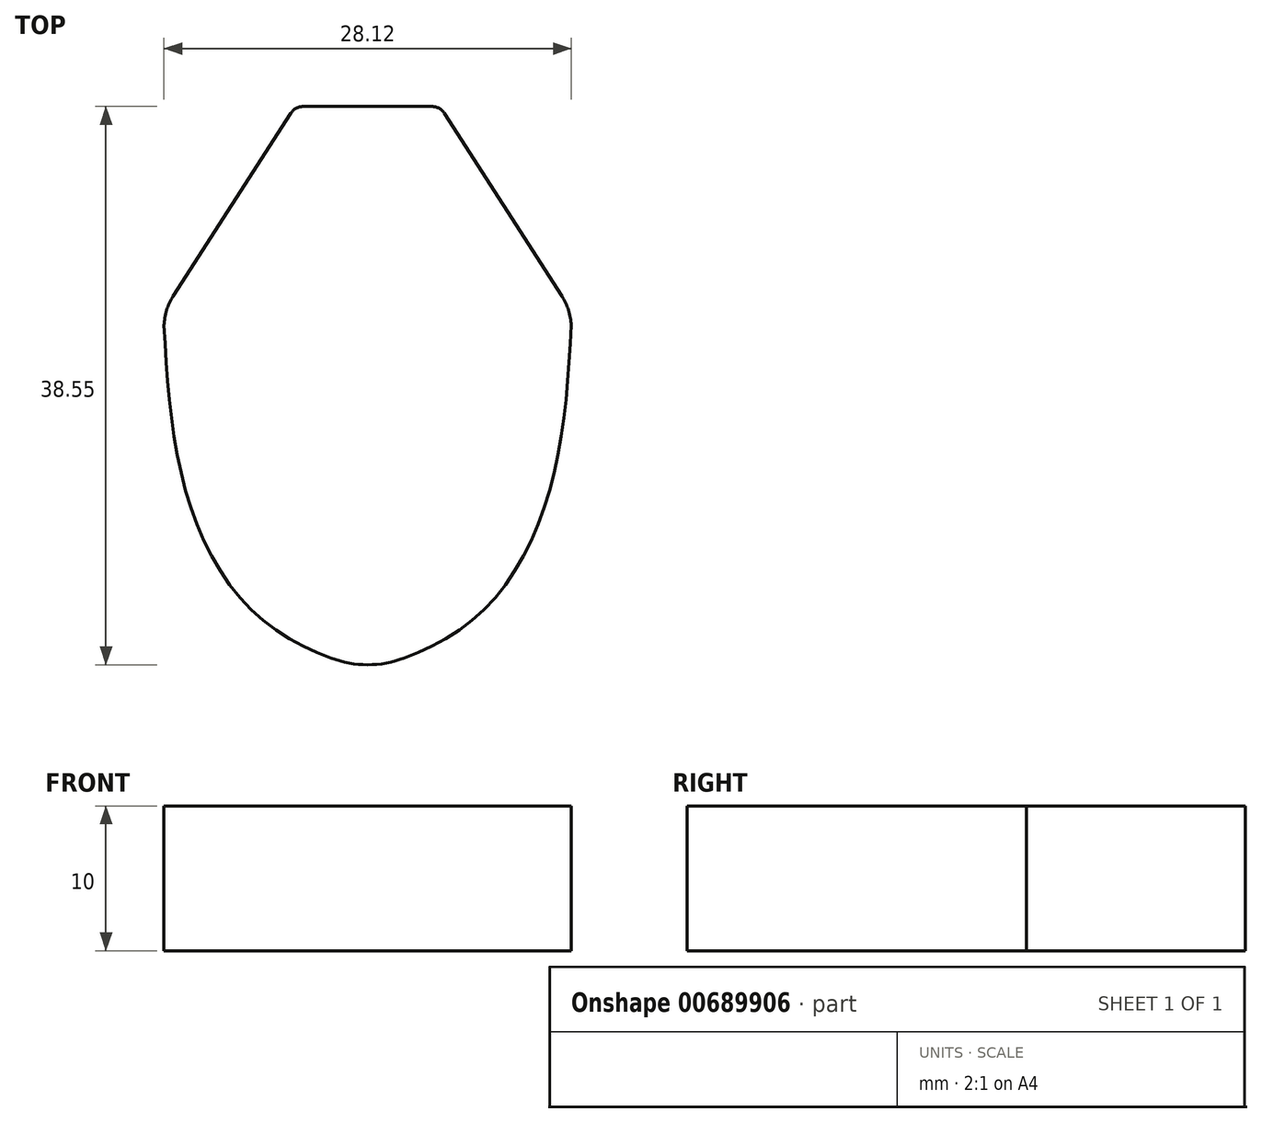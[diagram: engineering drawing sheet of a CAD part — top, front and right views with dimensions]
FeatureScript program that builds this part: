
annotation { "Feature Type Name" : "Feature", "Feature Type Description" : "" }
export const myFeature = defineFeature(function(context is Context, id is Id, definition is map)
    precondition{}
    {
        {
            var Q0;
            Q0=qCreatedBy(makeId("Top.planeOp"),FACE);
            var sketch = newSketch(context, id + "F0", { "sketchPlane" : qUnion([Q0])});
            skLineSegment(sketch, "E0", {"start": v(-13.42, 25.9) * mm, "end": v(-5.3, 38.54) * mm});
            skPoint(sketch, "E1.visualSharp", {"position": v(-5, 39) * mm});
            skArc(sketch, "E1.filletArc", {"start": v(-4.45, 39) * mm, "mid": v(-4.93, 38.88) * mm, "end": v(-5.3, 38.54) * mm});
            skPoint(sketch, "E2.visualSharp", {"position": v(-14, 25) * mm});
            skArc(sketch, "E2.filletArc", {"start": v(-13.42, 25.9) * mm, "mid": v(-13.88, 24.93) * mm, "end": v(-14.06, 23.89) * mm});
            skFitSpline(sketch, "E3", {"points": [v(-14.06, 23.89) * mm, v(-12.32, 11.64) * mm, v(-6.8, 3.17) * mm, v(0, 0) * mm], "startDerivative": vector(1.56, -32.92) * mm, "endDerivative": vector(18.5, -6.76) * mm});
            skArc(sketch, "E4.MirrorCS", {"start": v(13.42, 25.9) * mm, "mid": v(13.88, 24.93) * mm, "end": v(14.06, 23.89) * mm});
            skArc(sketch, "E5.MirrorCS", {"start": v(4.45, 39) * mm, "mid": v(4.93, 38.88) * mm, "end": v(5.3, 38.54) * mm});
            skFitSpline(sketch, "E6.MirrorCS", {"points": [v(14.06, 23.89) * mm, v(12.32, 11.64) * mm, v(6.8, 3.17) * mm, v(0, 0) * mm], "startDerivative": vector(-1.56, -32.92) * mm, "endDerivative": vector(-18.5, -6.76) * mm});
            skPoint(sketch, "E7.MirrorP", {"position": v(5, 39) * mm});
            skPoint(sketch, "E8.MirrorP", {"position": v(14, 25) * mm});
            skLineSegment(sketch, "E9.MirrorCS", {"start": v(13.42, 25.9) * mm, "end": v(5.3, 38.54) * mm});
            skLineSegment(sketch, "E10", {"start": v(-4.45, 39) * mm, "end": v(4.45, 39) * mm});
            skSolve(sketch);
        }
        {
            var Q0;
            Q0=makeQuery(id+"F0.imprint","IMPRINT",FACE,{"disambiguationData":[TD([[makeQuery(id+"F0.imprint","IMPRINT",EDGE,{"derivedFrom":sQuery(id+"F0.wireOp",EDGE,"E0")}),-1.0]])]});
            extrude(context, id + "F1", {"entities" : qUnion([Q0]), "depth" : 10 * mm, "offsetDistance" : 25 * mm});
        }
        {
            var Q0;
            Q0=makeQuery(id+"F1.opExtrude","SWEPT_EDGE",EDGE,{"disambiguationData":[OSD([sQuery(id+"F0.wireOp",EDGE,"E3"),sQuery(id+"F0.wireOp",EDGE,"E6.MirrorCS")])]});
            fillet(context, id + "F2", {"entities" : qUnion([Q0]), "radius" : 7 * mm, "tangentPropagation" : true, "allowEdgeOverflow" : false});
        }
    });
